# Revit family: INTONO C IN 3.8
name_source: partatom
category: Lighting Fixtures
units: mm (PartAtom-declared; Revit-internal decimal feet)

## family parameters
Always vertical = Yes
Cut with Voids When Loaded = No
Host = Ceiling
Light Source = Yes
OmniClass Number = 23.80.70.11
OmniClass Title = Luminaries for Internal Lighting
Part Type = Normal
Room Calculation Point = Yes
Round Connector Dimension = Use Diameter
Shared = No

## types (1)
- INTONO C IN 3.8 M 20° (3000K CRI90 9W 24Vdc)
    Body = L&L _Aluminium low copper
    CRI = CRI 80; CRI >90
    Code = -
    Color Filter = 16777215
    Control system = ON/OFF
    Cutout dimensions = -
    Default Elevation = 0 mm  [stored 0 ft]
    Delivered lumen output = 649 lm (3000K, 20°, CRI 90), 783 lm (3000K, 20°, CRI 80)
    Description = Ceiling mounted for indoor applications
    Dimming Lamp Color Temperature Shift = <None>
    Emit from Line Length = 609.6 mm  [stored 2 ft]
    Energy efficiency class = A A+ A++
    Features = easy installation thanks to 4-point magnetic fastener
    Height mm = 100 mm  [stored 0.328084 ft]
    Horizontal rotation max = 0.00°
    IP = IP40
    LED Colour = 2700K, 3000K, 4000K
    Length mm = 160 mm  [stored 0.524934 ft]
    Lens = L&L_Tempered extra-clear glass
    Lumen output at source = 822 lm (3000K, CRI 90), 988 lm (3000K, CRI 80)
    Manufacturer = L&L Luce&Light
    Material = Body in die-cast aluminium, screen in black-serigraphed, tempered, transparent extra-clear glass
    Model = Intono C IN 3.8
    Mounting = surface mounted (ceiling)
    No. and type of led = 1 high power density COB LED, 2-step MacAdam, 50 000h L95 B10 (Ta 25°C)
    Notes = Version compatible with Google Home or Amazon Echo available on request for voice command control
    Optics = 20°
    Photometric Web File = INTONO C 3.8 M 20° [3000K CRI90 9W 24Vdc].IES
    Power = 9W
    Power cables = -
    Power supply = 230Vac
    Power supply unit = not included
    Tilt Angle = -90.00°
    Trim = L&L_Black glass
    URL = https://www.lucelight.it
    URL Accessories and power supply units = https://www.lucelight.it
    URL Catalogue = https://www.lucelight.it
    URL DXF = https://www.lucelight.it
    URL Description = https://www.lucelight.it
    URL General code = https://www.lucelight.it
    URL IES Photometric file = https://www.lucelight.it
    URL Image = https://www.lucelight.it
    URL Technical sheet = -
    Vertical rotation max = 0.00°
    Weight kg = 1.15 kg
    Width mm = 85 mm  [stored 0.278871 ft]
    Wiring = -

note: [stored X ft] marks values corroborated as IEEE doubles in the binary element streams (Revit-internal decimal feet)

## geometry (parser evidence)
native form markers: Blend x4, Sweep x4
no freeform markers — native parametric forms only
